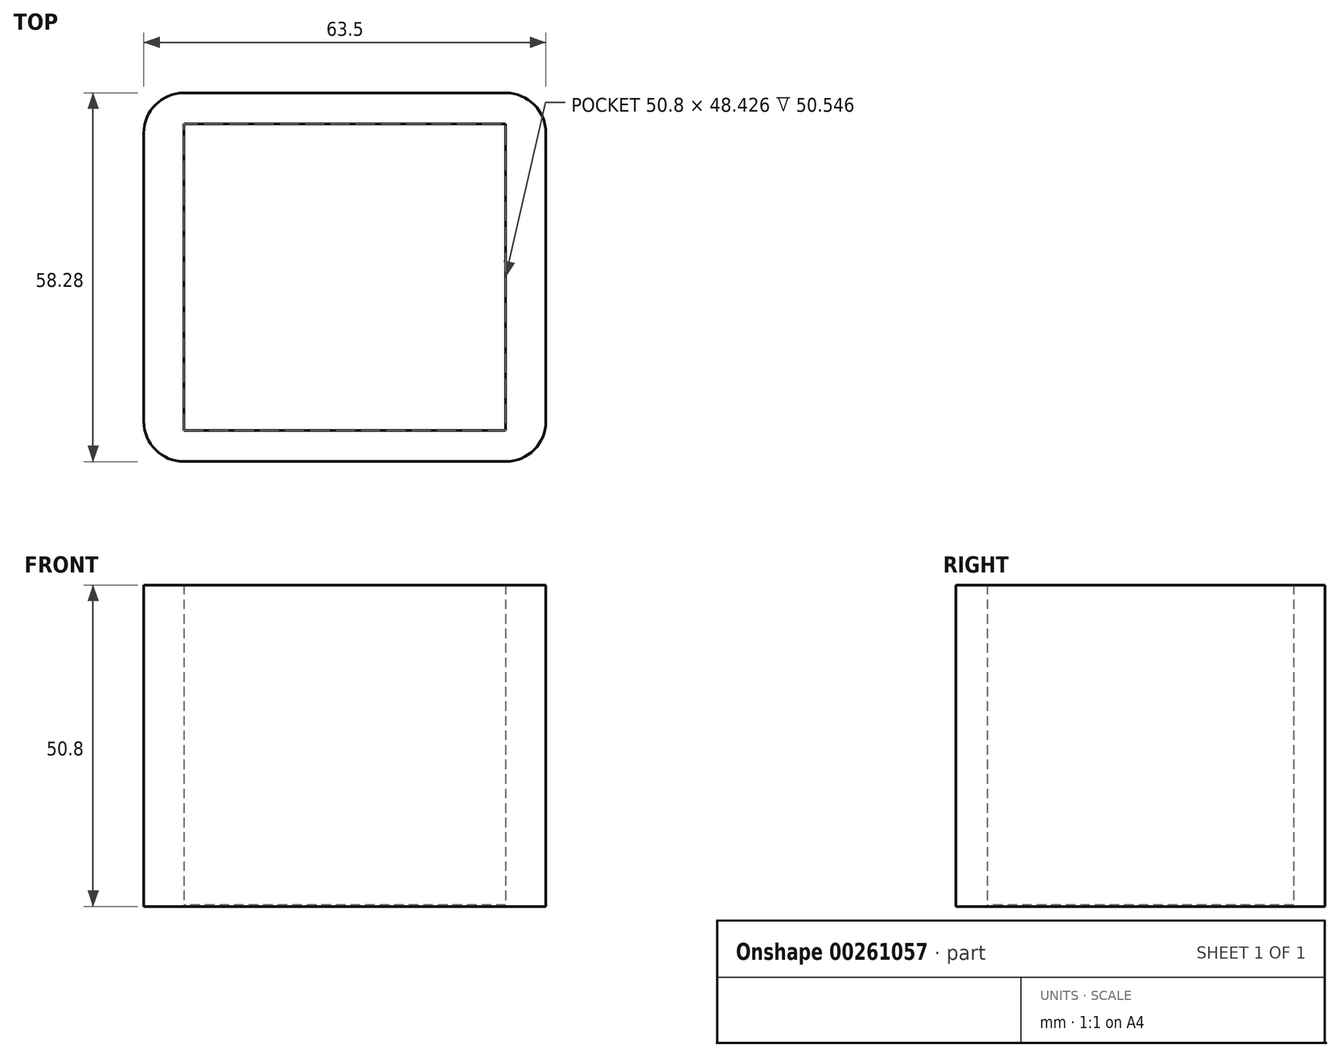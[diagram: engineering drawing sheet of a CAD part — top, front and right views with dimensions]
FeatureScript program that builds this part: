
annotation { "Feature Type Name" : "Feature", "Feature Type Description" : "" }
export const myFeature = defineFeature(function(context is Context, id is Id, definition is map)
    precondition{}
    {
        {
            var Q0;
            Q0=qCreatedBy(makeId("Top.planeOp"),FACE);
            var sketch = newSketch(context, id + "F0", { "sketchPlane" : qUnion([Q0])});
            skLineSegment(sketch, "E0.bottom", {"start": v(25.4, 29.14) * mm, "end": v(-25.4, 29.14) * mm});
            skLineSegment(sketch, "E0.top", {"start": v(25.4, -29.14) * mm, "end": v(-25.4, -29.14) * mm});
            skLineSegment(sketch, "E0.left", {"start": v(31.75, 22.79) * mm, "end": v(31.75, -22.79) * mm});
            skLineSegment(sketch, "E0.right", {"start": v(-31.75, 22.79) * mm, "end": v(-31.75, -22.79) * mm});
            skPoint(sketch, "E0.middle", {"position": v(0, 0) * mm});
            skLineSegment(sketch, "E1.bottom", {"start": v(25.4, 24.21) * mm, "end": v(-25.4, 24.21) * mm});
            skLineSegment(sketch, "E1.top", {"start": v(25.4, -24.21) * mm, "end": v(-25.4, -24.21) * mm});
            skLineSegment(sketch, "E1.left", {"start": v(25.4, 24.21) * mm, "end": v(25.4, -24.21) * mm});
            skLineSegment(sketch, "E1.right", {"start": v(-25.4, 24.21) * mm, "end": v(-25.4, -24.21) * mm});
            skPoint(sketch, "E2.visualSharp", {"position": v(31.75, 29.14) * mm});
            skArc(sketch, "E2.filletArc", {"start": v(31.75, 22.79) * mm, "mid": v(29.9, 27.28) * mm, "end": v(25.4, 29.14) * mm});
            skPoint(sketch, "E3.visualSharp", {"position": v(31.75, -29.14) * mm});
            skArc(sketch, "E3.filletArc", {"start": v(25.4, -29.14) * mm, "mid": v(29.9, -27.28) * mm, "end": v(31.75, -22.79) * mm});
            skPoint(sketch, "E4.visualSharp", {"position": v(-31.75, -29.14) * mm});
            skArc(sketch, "E4.filletArc", {"start": v(-31.75, -22.79) * mm, "mid": v(-29.9, -27.28) * mm, "end": v(-25.4, -29.14) * mm});
            skPoint(sketch, "E5.visualSharp", {"position": v(-31.75, 29.14) * mm});
            skArc(sketch, "E5.filletArc", {"start": v(-25.4, 29.14) * mm, "mid": v(-29.9, 27.28) * mm, "end": v(-31.75, 22.79) * mm});
            skSolve(sketch);
        }
        {
            var Q0;
            Q0 = qSketchRegion(id + "F0", true);
            extrude(context, id + "F1", {"entities" : qUnion([Q0]), "depth" : 50.8 * mm});
        }
        {
            var Q0;
            Q0=qCreatedBy(makeId("Top.planeOp"),FACE);
            var sketch = newSketch(context, id + "F2", { "sketchPlane" : qUnion([Q0])});
            skLineSegment(sketch, "E6.bottom", {"start": v(25.78, -24.89) * mm, "end": v(-25.78, -24.89) * mm});
            skLineSegment(sketch, "E6.top", {"start": v(25.78, 24.89) * mm, "end": v(-25.78, 24.89) * mm});
            skLineSegment(sketch, "E6.left", {"start": v(25.78, -24.89) * mm, "end": v(25.78, 24.89) * mm});
            skLineSegment(sketch, "E6.right", {"start": v(-25.78, -24.89) * mm, "end": v(-25.78, 24.89) * mm});
            skPoint(sketch, "E6.middle", {"position": v(0, 0) * mm});
            skSolve(sketch);
        }
        {
            var Q0;
            Q0 = qSketchRegion(id + "F2", true);
            extrude(context, id + "F3", {"entities" : qUnion([Q0]), "operationType" : NewBodyOperationType.ADD, "depth" : 0.25 * mm});
        }
    });
